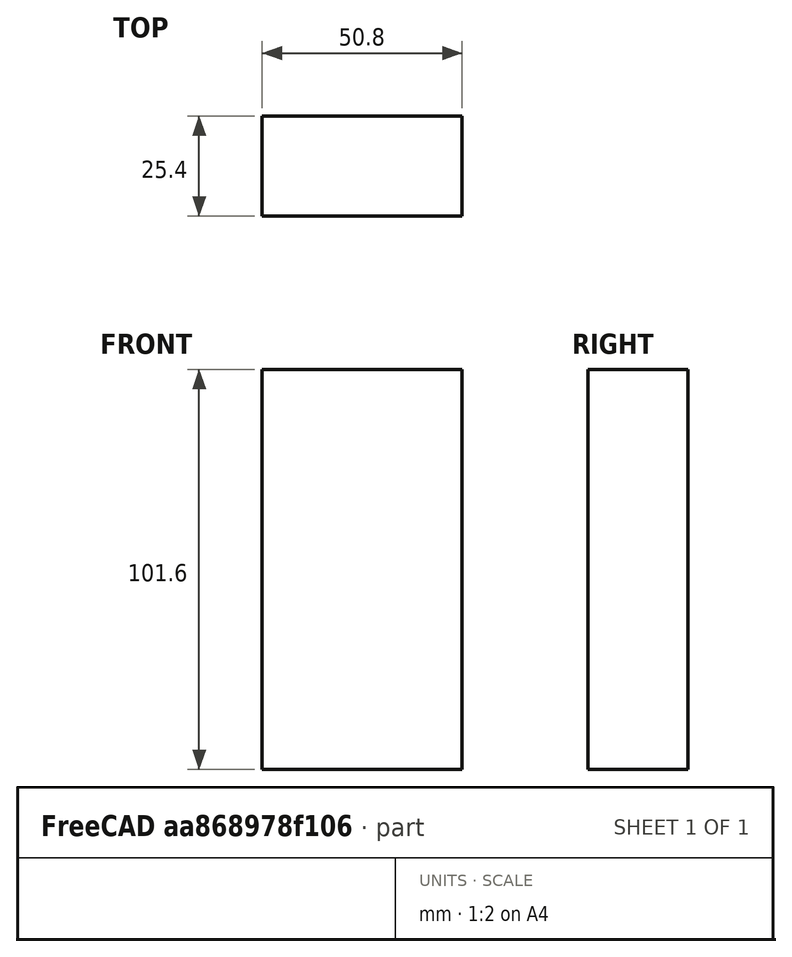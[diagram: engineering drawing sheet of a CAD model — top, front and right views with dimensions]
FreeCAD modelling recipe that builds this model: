
FCSTD DOCUMENT  (FreeCAD 0.19R24276 (Git))
Label: leg stud
License: All rights reserved
LicenseURL: http://en.wikipedia.org/wiki/All_rights_reserved
objects: Sketcher::SketchObject×1, PartDesign::Pad×1, PartDesign::Body×1
note: 4 computed .brp shape members not serialized (recipe doc carries the construction recipe); baked Part::Feature solids carry a one-line shape summary decoded from their .brp

FEATURE [Sketcher::SketchObject] Sketch
  FullyConstrained = true
  MapMode = 5
  Placement = pos=(0,0,0) rot=(1,0,0;1.5708rad)
  Support = -> [XZ_Plane]
  sketch-geometry (4):
    g0: LineSegment StartX=0 StartY=0 StartZ=0 EndX=50.8 EndY=0 EndZ=0
    g1: LineSegment StartX=50.8 StartY=0 StartZ=0 EndX=50.8 EndY=101.6 EndZ=0
    g2: LineSegment StartX=50.8 StartY=101.6 StartZ=0 EndX=0 EndY=101.6 EndZ=0
    g3: LineSegment StartX=0 StartY=101.6 StartZ=0 EndX=0 EndY=0 EndZ=0
  constraints (11):
    c: Coincident(g0,g1)
    c: Coincident(g1,g2)
    c: Coincident(g2,g3)
    c: Coincident(g3,g0)
    c: Horizontal(g0)
    c: Horizontal(g2)
    c: Vertical(g1)
    c: Vertical(g3)
    c: Coincident(g0,g-1)
    c: DistanceY(g1,g1) = 101.6
    c: DistanceX(g0,g0) = 50.8
FEATURE [PartDesign::Pad] Pad
  Direction = (1,1,1)
  Length = 12.7
  Length2 = 100
  Placement = pos=(0,0,0) rot=(1,0,0;1.5708rad)
  Profile = -> Sketch
  Type = 0
FEATURE [PartDesign::Body] Body
  Group = -> [Sketch,Pad]
  Origin = -> Origin
  Tip = -> Pad
